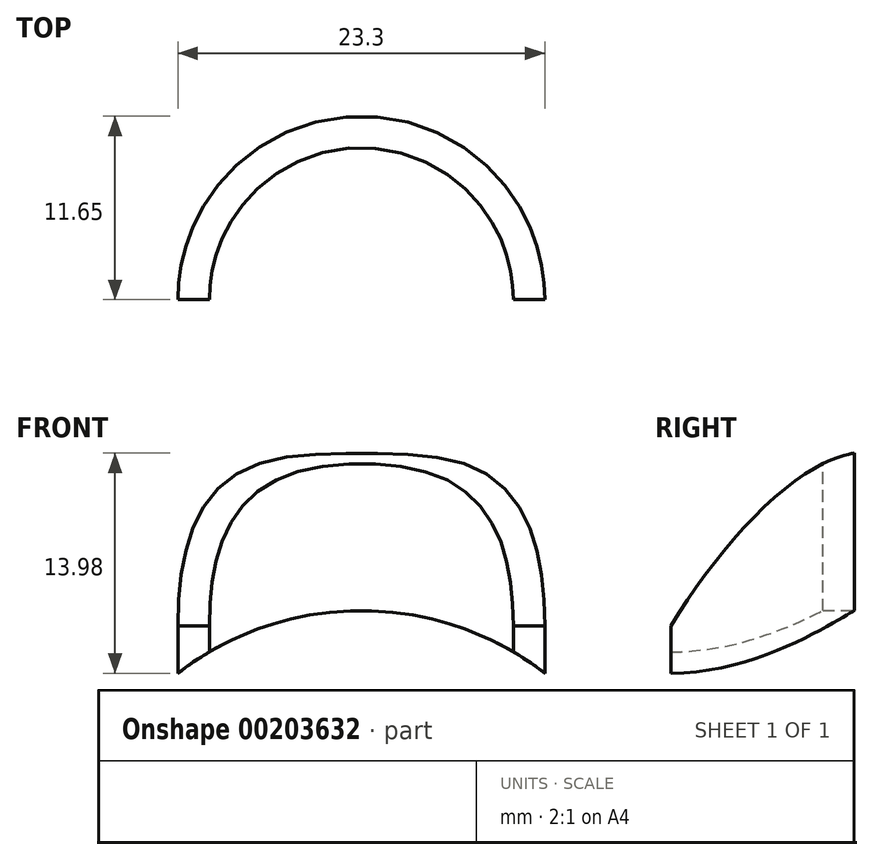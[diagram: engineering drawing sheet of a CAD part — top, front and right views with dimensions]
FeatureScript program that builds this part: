
annotation { "Feature Type Name" : "Feature", "Feature Type Description" : "" }
export const myFeature = defineFeature(function(context is Context, id is Id, definition is map)
    precondition{}
    {
        {
            var Q0;
            Q0=qCreatedBy(makeId("Front.planeOp"),FACE);
            var sketch = newSketch(context, id + "F0", { "sketchPlane" : qUnion([Q0])});
            skCircle(sketch, "E0", {"center": v(0, 0) * mm, "radius": 19.05 * mm});
            skLineSegment(sketch, "E1.bottom", {"start": v(-19.05, 0.01) * mm, "end": v(19.05, 0.01) * mm});
            skLineSegment(sketch, "E1.top", {"start": v(-19.05, 29.05) * mm, "end": v(19.05, 29.05) * mm});
            skLineSegment(sketch, "E1.left", {"start": v(-19.05, 0.01) * mm, "end": v(-19.05, 29.05) * mm});
            skLineSegment(sketch, "E1.right", {"start": v(19.05, 0.01) * mm, "end": v(19.05, 29.05) * mm});
            skSolve(sketch);
        }
        {
            var Q0;
            Q0=makeQuery(id+"F0.imprint","IMPRINT",FACE,{"disambiguationData":[TD([[makeQuery(id+"F0.imprint","IMPRINT",EDGE,{"derivedFrom":sQuery(id+"F0.wireOp",EDGE,"E1.top")}),-1.0]])]});
            extrude(context, id + "F1", {"entities" : qUnion([Q0]), "depth" : 25 * mm});
        }
        {
            var Q0;
            Q0=makeQuery(id+"F1.opExtrude","SWEPT_FACE",FACE,{"disambiguationData":[OSD([sQuery(id+"F0.wireOp",EDGE,"E1.top")])]});
            var sketch = newSketch(context, id + "F2", { "sketchPlane" : qUnion([Q0])});
            skArc(sketch, "E2", {"start": v(11.65, -16) * mm, "mid": v(0, -4.35) * mm, "end": v(-11.65, -16) * mm});
            skArc(sketch, "E3.0", {"start": v(9.65, -16) * mm, "mid": v(0, -6.35) * mm, "end": v(-9.65, -16) * mm});
            skLineSegment(sketch, "E4", {"start": v(-11.65, -16) * mm, "end": v(-9.65, -16) * mm});
            skLineSegment(sketch, "E5.trimOffspring", {"start": v(9.65, -16) * mm, "end": v(11.65, -16) * mm});
            skLineSegment(sketch, "E6.0", {"start": v(-19.05, 0) * mm, "end": v(19.05, 0) * mm});
            skLineSegment(sketch, "E7.0", {"start": v(-19.05, -25) * mm, "end": v(-19.05, 0) * mm});
            skLineSegment(sketch, "E7.1", {"start": v(-19.05, -25) * mm, "end": v(19.05, -25) * mm});
            skLineSegment(sketch, "E7.2", {"start": v(19.05, -25) * mm, "end": v(19.05, 0) * mm});
            skSolve(sketch);
        }
        {
            var Q0;
            Q0 = qSketchRegion(id + "F2", true);
            extrude(context, id + "F3", {"entities" : qUnion([Q0]), "operationType" : NewBodyOperationType.REMOVE, "endBound" : BoundingType.THROUGH_ALL, "oppositeDirection" : true, "depth" : 25 * mm});
        }
        {
            var Q0;
            Q0=qCreatedBy(makeId("Right.planeOp"),FACE);
            var sketch = newSketch(context, id + "F4", { "sketchPlane" : qUnion([Q0])});
            skLineSegment(sketch, "E8.0", {"start": v(-16, 15.07) * mm, "end": v(-16, 29.05) * mm});
            skLineSegment(sketch, "E8.1", {"start": v(-16, 29.05) * mm, "end": v(-4.35, 29.05) * mm});
            skFitSpline(sketch, "E9", {"points": [v(-16, 18.07) * mm, v(-4.35, 29.05) * mm], "startDerivative": vector(7.6, 12.7) * mm, "endDerivative": vector(12.46, 1.88) * mm});
            skSolve(sketch);
        }
        {
            var Q0;
            Q0 = qSketchRegion(id + "F4", true);
            extrude(context, id + "F5", {"entities" : qUnion([Q0]), "operationType" : NewBodyOperationType.REMOVE, "endBound" : BoundingType.THROUGH_ALL, "oppositeDirection" : true, "depth" : 25 * mm, "hasSecondDirection" : true, "secondDirectionBound" : SecondDirectionBoundingType.THROUGH_ALL, "secondDirectionOppositeDirection" : false, "secondDirectionDepth" : 25 * mm});
        }
    });
